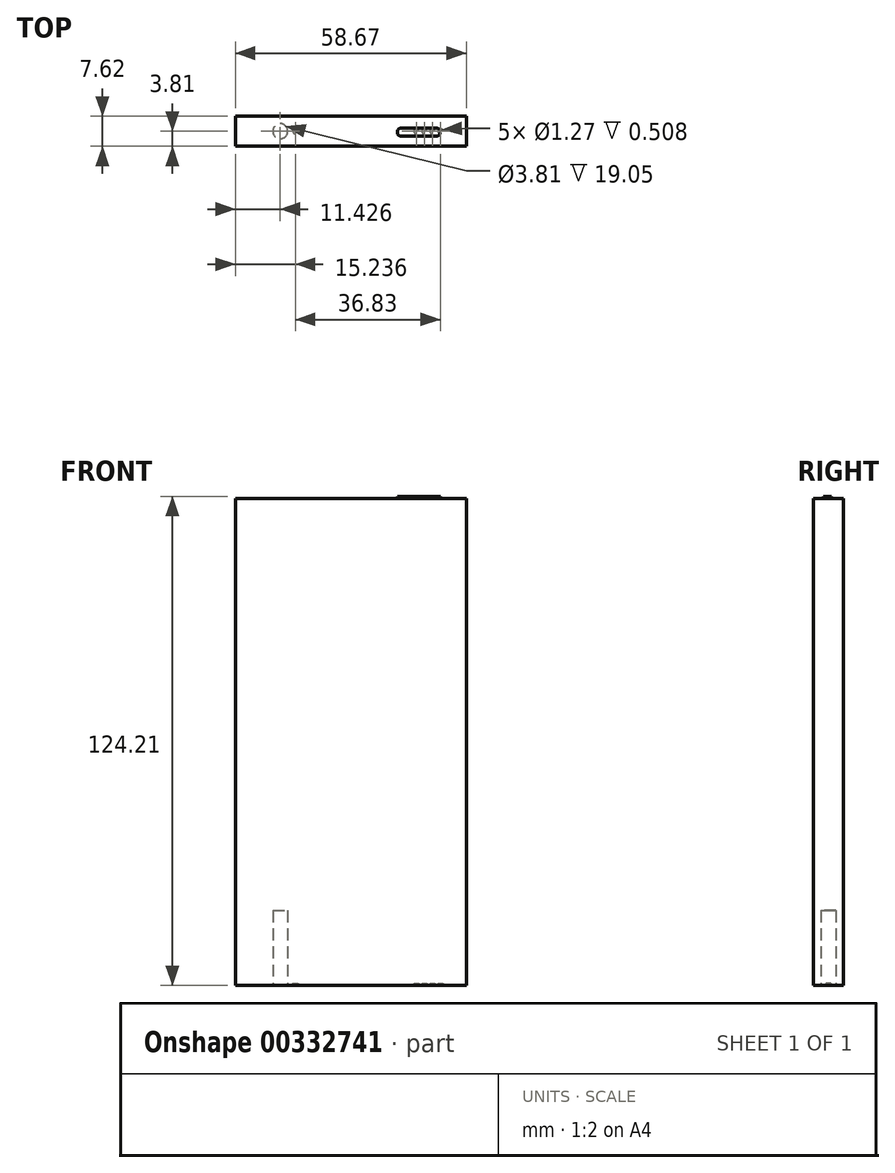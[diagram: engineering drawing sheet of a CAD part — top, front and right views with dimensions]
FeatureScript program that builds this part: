
annotation { "Feature Type Name" : "Feature", "Feature Type Description" : "" }
export const myFeature = defineFeature(function(context is Context, id is Id, definition is map)
    precondition{}
    {
        {
            var Q0;
            Q0=qCreatedBy(makeId("Front.planeOp"),FACE);
            var sketch = newSketch(context, id + "F0", { "sketchPlane" : qUnion([Q0])});
            skLineSegment(sketch, "E0.bottom", {"start": v(0, 0) * mm, "end": v(-58.67, 0) * mm});
            skLineSegment(sketch, "E0.top", {"start": v(0, 123.7) * mm, "end": v(-58.67, 123.7) * mm});
            skLineSegment(sketch, "E0.left", {"start": v(0, 0) * mm, "end": v(0, 123.7) * mm});
            skLineSegment(sketch, "E0.right", {"start": v(-58.67, 0) * mm, "end": v(-58.67, 123.7) * mm});
            skSolve(sketch);
        }
        {
            var Q0;
            Q0=makeQuery(id+"F0.imprint","IMPRINT",FACE,{"disambiguationData":[TD([[makeQuery(id+"F0.imprint","IMPRINT",EDGE,{"derivedFrom":sQuery(id+"F0.wireOp",EDGE,"E0.bottom")}),-1.0]])]});
            extrude(context, id + "F1", {"entities" : qUnion([Q0]), "depth" : 7.62 * mm});
        }
        {
            var Q0;
            Q0=makeQuery(id+"F1.opExtrude","SWEPT_FACE",FACE,{"disambiguationData":[OSD([sQuery(id+"F0.wireOp",EDGE,"E0.top")])]});
            var sketch = newSketch(context, id + "F2", { "sketchPlane" : qUnion([Q0])});
            skLineSegment(sketch, "E1.bottom", {"start": v(-16.51, -5.08) * mm, "end": v(-7.62, -5.08) * mm});
            skLineSegment(sketch, "E1.top", {"start": v(-16.51, -3.05) * mm, "end": v(-7.62, -3.05) * mm});
            skLineSegment(sketch, "E1.left", {"start": v(-16.51, -5.08) * mm, "end": v(-16.51, -3.05) * mm});
            skLineSegment(sketch, "E1.right", {"start": v(-7.62, -5.08) * mm, "end": v(-7.62, -3.05) * mm});
            skCircle(sketch, "E2", {"center": v(-16.51, -4.06) * mm, "radius": 1.02 * mm});
            skCircle(sketch, "E3", {"center": v(-7.62, -4.06) * mm, "radius": 1.02 * mm});
            skSolve(sketch);
        }
        {
            var Q0;
            Q0 = qSketchRegion(id + "F2", true);
            extrude(context, id + "F3", {"entities" : qUnion([Q0]), "operationType" : NewBodyOperationType.ADD, "depth" : 0.5 * mm});
        }
        {
            var Q0;
            Q0=makeQuery(id+"F1.opExtrude","SWEPT_FACE",FACE,{"disambiguationData":[OSD([sQuery(id+"F0.wireOp",EDGE,"E0.bottom")])]});
            var sketch = newSketch(context, id + "F4", { "sketchPlane" : qUnion([Q0])});
            skCircle(sketch, "E4", {"center": v(-47.24, 3.81) * mm, "radius": 1.9 * mm});
            skSolve(sketch);
        }
        {
            var Q0;
            Q0=makeQuery(id+"F4.imprint","IMPRINT",FACE,{"disambiguationData":[TD([[makeQuery(id+"F4.imprint","IMPRINT",EDGE,{"derivedFrom":sQuery(id+"F4.wireOp",EDGE,"E4")}),1.0]])]});
            extrude(context, id + "F5", {"entities" : qUnion([Q0]), "operationType" : NewBodyOperationType.REMOVE, "oppositeDirection" : true, "depth" : 19.05 * mm});
        }
        {
            var Q0;
            Q0=makeQuery(id+"F1.opExtrude","SWEPT_FACE",FACE,{"disambiguationData":[OSD([sQuery(id+"F0.wireOp",EDGE,"E0.bottom")])]});
            var sketch = newSketch(context, id + "F6", { "sketchPlane" : qUnion([Q0])});
            skCircle(sketch, "E5", {"center": v(-43.43, 3.81) * mm, "radius": 0.64 * mm});
            skCircle(sketch, "E6", {"center": v(-12.7, 3.81) * mm, "radius": 0.64 * mm});
            skCircle(sketch, "E7.1.0.0", {"center": v(-10.67, 3.81) * mm, "radius": 0.64 * mm});
            skCircle(sketch, "E7.2.0.0", {"center": v(-8.64, 3.81) * mm, "radius": 0.64 * mm});
            skLineSegment(sketch, "E7.direction1", {"start": v(-12.7, 3.81) * mm, "end": v(-10.67, 3.81) * mm, "construction": true});
            skCircle(sketch, "E8.0.3.0", {"center": v(-6.6, 3.81) * mm, "radius": 0.64 * mm});
            skSolve(sketch);
        }
        {
            var Q0;
            Q0 = qSketchRegion(id + "F6", true);
            extrude(context, id + "F7", {"entities" : qUnion([Q0]), "operationType" : NewBodyOperationType.REMOVE, "oppositeDirection" : true, "depth" : 0.5 * mm});
        }
    });
